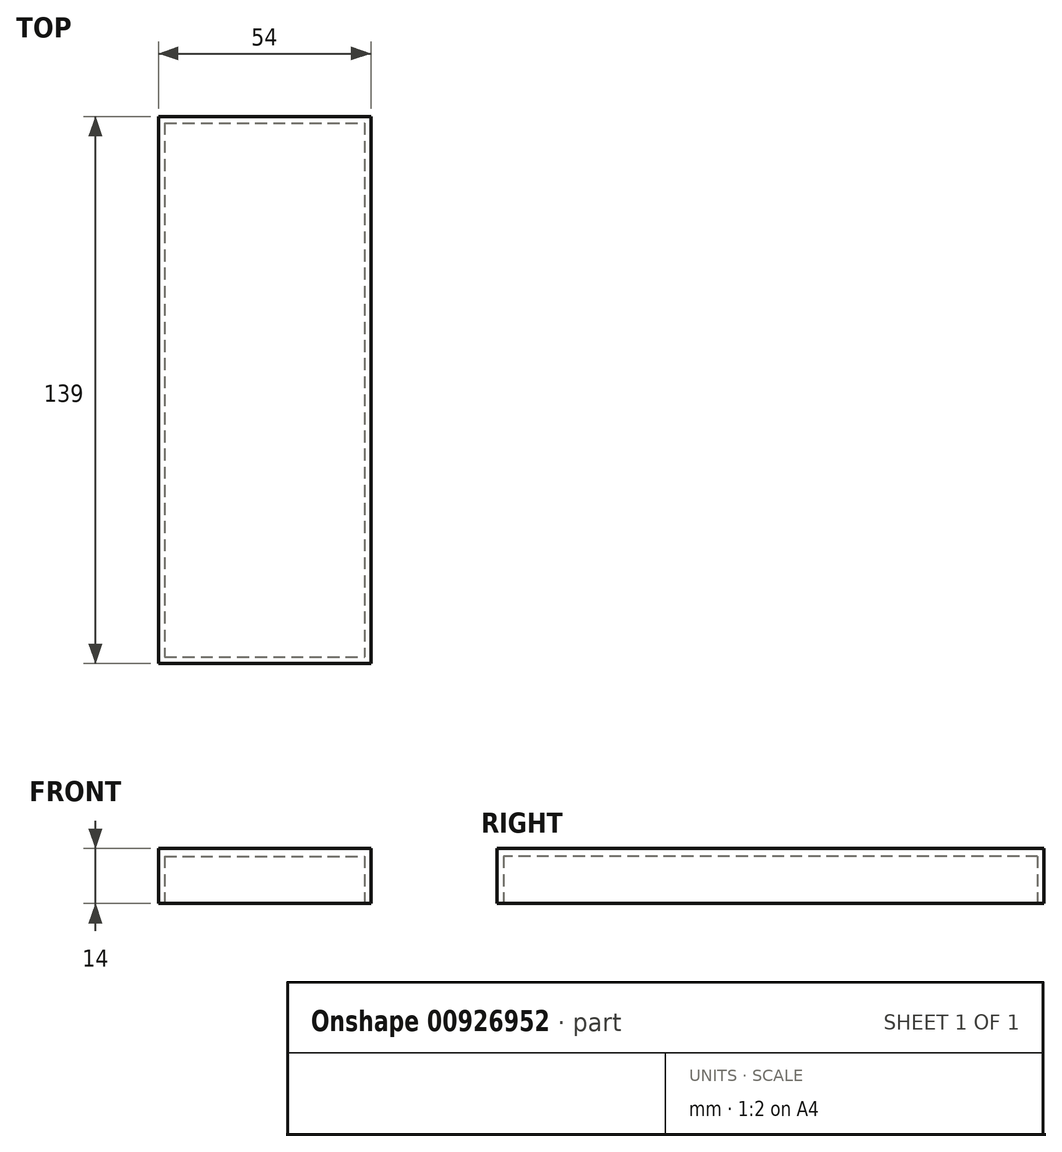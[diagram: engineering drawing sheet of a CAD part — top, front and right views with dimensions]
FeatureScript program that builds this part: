
annotation { "Feature Type Name" : "Feature", "Feature Type Description" : "" }
export const myFeature = defineFeature(function(context is Context, id is Id, definition is map)
    precondition{}
    {
        {
            var Q0;
            Q0=qCreatedBy(makeId("Top.planeOp"),FACE);
            var sketch = newSketch(context, id + "F0", { "sketchPlane" : qUnion([Q0])});
            skLineSegment(sketch, "E0.bottom", {"start": v(-25.4, 67.85) * mm, "end": v(25.4, 67.85) * mm});
            skLineSegment(sketch, "E0.top", {"start": v(-25.4, -67.85) * mm, "end": v(25.4, -67.85) * mm});
            skLineSegment(sketch, "E0.left", {"start": v(-25.4, 67.85) * mm, "end": v(-25.4, -67.85) * mm});
            skLineSegment(sketch, "E0.right", {"start": v(25.4, 67.85) * mm, "end": v(25.4, -67.85) * mm});
            skPoint(sketch, "E0.middle", {"position": v(0, 0) * mm});
            skSolve(sketch);
        }
        {
            var Q0;
            Q0=qCreatedBy(makeId("Top.planeOp"),FACE);
            var sketch = newSketch(context, id + "F1", { "sketchPlane" : qUnion([Q0])});
            skLineSegment(sketch, "E1.bottom", {"start": v(-27, 69.5) * mm, "end": v(27, 69.5) * mm});
            skLineSegment(sketch, "E1.top", {"start": v(-27, -69.5) * mm, "end": v(27, -69.5) * mm});
            skLineSegment(sketch, "E1.left", {"start": v(-27, 69.5) * mm, "end": v(-27, -69.5) * mm});
            skLineSegment(sketch, "E1.right", {"start": v(27, 69.5) * mm, "end": v(27, -69.5) * mm});
            skPoint(sketch, "E1.middle", {"position": v(0, 0) * mm});
            skSolve(sketch);
        }
        {
            var Q0;
            Q0 = qSketchRegion(id + "F1", true);
            extrude(context, id + "F2", {"entities" : qUnion([Q0]), "depth" : 14 * mm, "offsetDistance" : 25 * mm});
        }
        {
            var Q0;
            Q0 = qSketchRegion(id + "F0", true);
            extrude(context, id + "F3", {"entities" : qUnion([Q0]), "operationType" : NewBodyOperationType.REMOVE, "depth" : 12 * mm, "offsetDistance" : 25 * mm});
        }
    });
